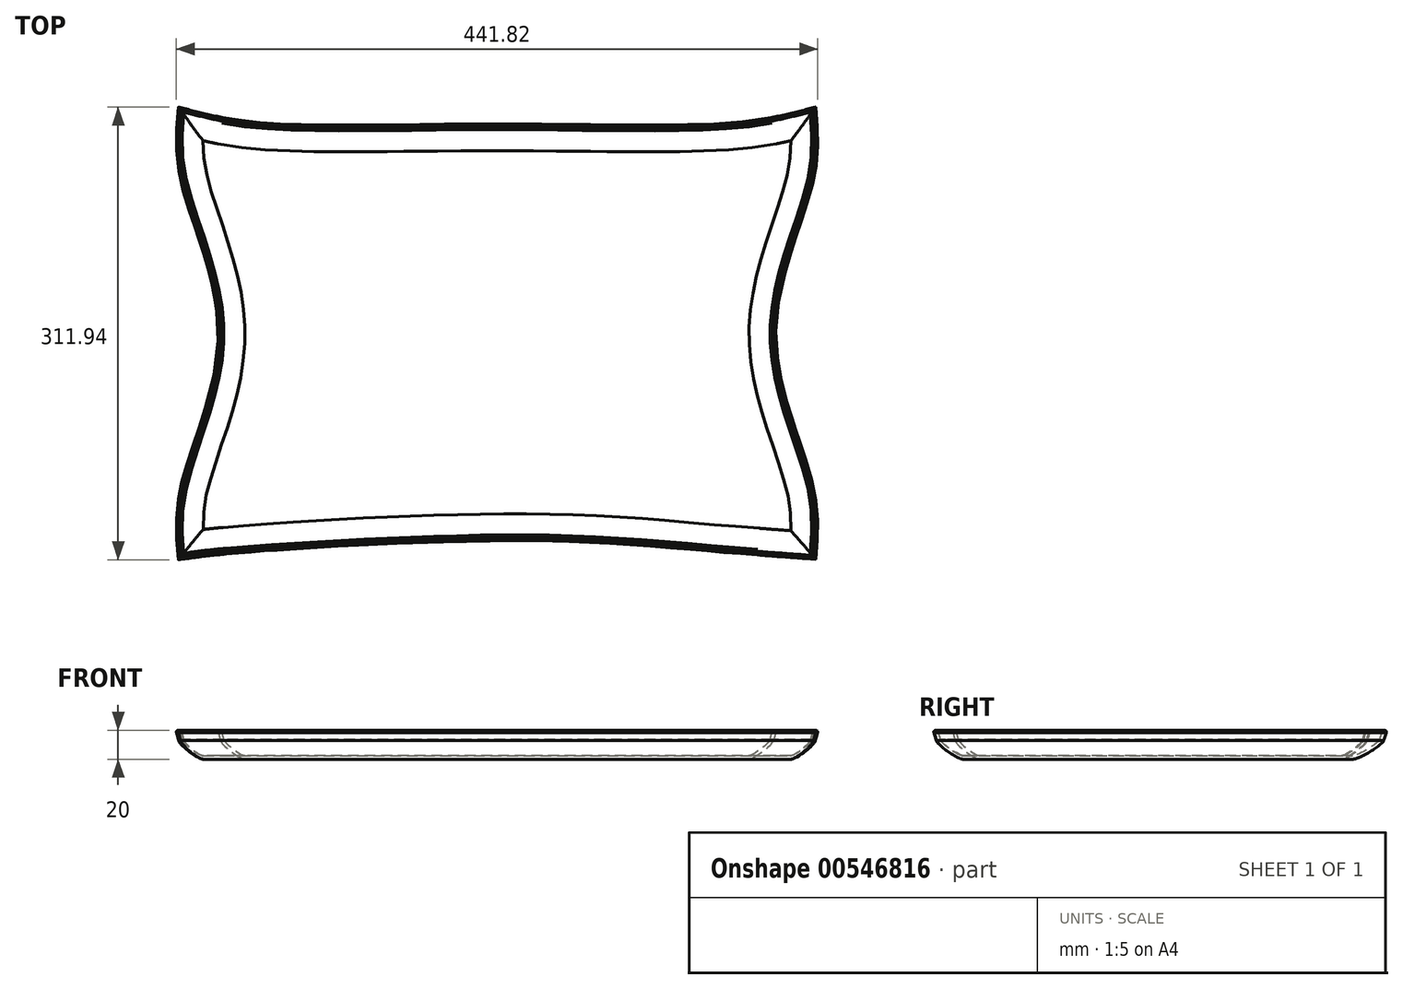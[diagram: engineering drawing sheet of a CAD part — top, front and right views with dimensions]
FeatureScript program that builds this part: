
annotation { "Feature Type Name" : "Feature", "Feature Type Description" : "" }
export const myFeature = defineFeature(function(context is Context, id is Id, definition is map)
    precondition{}
    {
        {
            var Q0;
            Q0=qCreatedBy(makeId("Top.planeOp"),FACE);
            var sketch = newSketch(context, id + "F0", { "sketchPlane" : qUnion([Q0])});
            skFitSpline(sketch, "E0", {"points": [v(-215, 150) * mm, v(-200, 0) * mm, v(-215, -150) * mm], "startDerivative": vector(12.45, -265.1) * mm, "endDerivative": vector(-12.45, -265.1) * mm});
            skLineSegment(sketch, "E1", {"start": v(0, 0) * mm, "end": v(-102.7, 0) * mm, "construction": true});
            skLineSegment(sketch, "E2", {"start": v(0, 0) * mm, "end": v(0, 245.04) * mm, "construction": true});
            skFitSpline(sketch, "E3.MirrorCS", {"points": [v(215, 150) * mm, v(200, 0) * mm, v(215, -150) * mm], "startDerivative": vector(-12.45, -265.1) * mm, "endDerivative": vector(12.45, -265.1) * mm});
            skFitSpline(sketch, "E4", {"points": [v(-215, 150) * mm, v(0, 140.22) * mm, v(215, 150) * mm], "startDerivative": vector(302.65, -55.49) * mm, "endDerivative": vector(302.65, 55.49) * mm});
            skFitSpline(sketch, "E5", {"points": [v(-215, -150) * mm, v(0, -141.43) * mm, v(215, -150) * mm], "startDerivative": vector(199.47, 22.4) * mm, "endDerivative": vector(430, -33.3) * mm});
            skPoint(sketch, "E6", {"position": v(0, 122.52) * mm});
            skSolve(sketch);
        }
        {
            var Q0;
            Q0=qCreatedBy(makeId("Top.planeOp"),FACE);
            var sketch = newSketch(context, id + "F1", { "sketchPlane" : qUnion([Q0])});
            skFitSpline(sketch, "E7.0", {"points": [v(215, -150) * mm, v(212.93, -105.82) * mm, v(187.07, 0) * mm, v(212.93, 105.82) * mm, v(215, 150) * mm]});
            skFitSpline(sketch, "E7.1", {"points": [v(-215, -150) * mm, v(-181.76, -146.27) * mm, v(19.21, -137.5) * mm, v(143.33, -144.45) * mm, v(215, -150) * mm]});
            skFitSpline(sketch, "E7.2", {"points": [v(-215, 150) * mm, v(-212.93, 105.82) * mm, v(-187.07, 0) * mm, v(-212.93, -105.82) * mm, v(-215, -150) * mm]});
            skFitSpline(sketch, "E7.3", {"points": [v(215, 150) * mm, v(164.56, 140.75) * mm, v(0, 139.68) * mm, v(-164.56, 140.75) * mm, v(-215, 150) * mm]});
            skPoint(sketch, "E8.visualSharp", {"position": v(215, 150) * mm});
            skArc(sketch, "E8.filletArc", {"start": v(211.29, 111.47) * mm, "mid": v(203.11, 136.17) * mm, "end": v(178.71, 145.2) * mm});
            skPoint(sketch, "E9.visualSharp", {"position": v(215, -150) * mm});
            skArc(sketch, "E9.filletArc", {"start": v(179.73, -147.4) * mm, "mid": v(203.62, -138.07) * mm, "end": v(211.57, -113.69) * mm});
            skPoint(sketch, "E10.visualSharp", {"position": v(-215, -150) * mm});
            skArc(sketch, "E10.filletArc", {"start": v(-211.54, -113.48) * mm, "mid": v(-203.67, -137.8) * mm, "end": v(-179.93, -147.22) * mm});
            skPoint(sketch, "E11.visualSharp", {"position": v(-215, 150) * mm});
            skArc(sketch, "E11.filletArc", {"start": v(-178.71, 145.2) * mm, "mid": v(-203.11, 136.17) * mm, "end": v(-211.29, 111.47) * mm});
            skSolve(sketch);
        }
        {
            var Q0;
            Q0=qCreatedBy(makeId("Front.planeOp"),FACE);
            var sketch = newSketch(context, id + "F2", { "sketchPlane" : qUnion([Q0])});
            skFitSpline(sketch, "E12", {"points": [v(-200, 0) * mm, v(-188.06, -11.18) * mm, v(0, -22.58) * mm], "startDerivative": vector(27.31, -89.51) * mm, "endDerivative": vector(299, 3.02) * mm});
            skLineSegment(sketch, "E13", {"start": v(0, 0) * mm, "end": v(0, -66.44) * mm, "construction": true});
            skFitSpline(sketch, "E14.MirrorCS", {"points": [v(200, 0) * mm, v(188.06, -11.18) * mm, v(0, -22.58) * mm], "startDerivative": vector(-27.31, -89.51) * mm, "endDerivative": vector(-299, 3.02) * mm});
            skSolve(sketch);
        }
        {
            var Q0;
            Q0 = qSketchRegion(id + "F1", true);
            extrude(context, id + "F3", {"entities" : qUnion([Q0]), "depth" : 20 * mm, "offsetDistance" : 25 * mm, "hasDraft" : true, "draftAngle" : 15 * degree});
        }
        {
            var Q0;
            Q0=makeQuery(id+"F3.opExtrude","CAP_FACE",FACE,{"disambiguationData":[OSD([sQuery(id+"F1.wireOp",EDGE,"E7.0"),sQuery(id+"F1.wireOp",EDGE,"E7.1"),sQuery(id+"F1.wireOp",EDGE,"E7.2"),sQuery(id+"F1.wireOp",EDGE,"E7.3"),sQuery(id+"F1.wireOp",EDGE,"E8.filletArc"),sQuery(id+"F1.wireOp",EDGE,"E9.filletArc"),sQuery(id+"F1.wireOp",EDGE,"E10.filletArc"),sQuery(id+"F1.wireOp",EDGE,"E11.filletArc")])],"isStart":false});
            shell(context, id + "F4", {"entities" : qUnion([Q0]), "thickness" : 2.5 * mm});
        }
        {
            var Q0;
            Q0=makeQuery(id+"F4.opShell","OFFSET_FACE",FACE,{"disambiguationData":[OSD([sQuery(id+"F1.wireOp",EDGE,"E7.0"),sQuery(id+"F1.wireOp",EDGE,"E7.1"),sQuery(id+"F1.wireOp",EDGE,"E7.2"),sQuery(id+"F1.wireOp",EDGE,"E7.3"),sQuery(id+"F1.wireOp",EDGE,"E8.filletArc"),sQuery(id+"F1.wireOp",EDGE,"E9.filletArc"),sQuery(id+"F1.wireOp",EDGE,"E10.filletArc"),sQuery(id+"F1.wireOp",EDGE,"E11.filletArc")])]});
            fillet(context, id + "F5", {"entities" : qUnion([Q0]), "radius" : 15 * mm, "tangentPropagation" : true, "rho" : 0.2, "crossSection" : FilletCrossSection.CONIC, "allowEdgeOverflow" : false});
        }
        {
            var Q0;
            Q0=makeQuery(id+"F3.opExtrude","CAP_FACE",FACE,{"disambiguationData":[OSD([sQuery(id+"F1.wireOp",EDGE,"E7.0"),sQuery(id+"F1.wireOp",EDGE,"E7.1"),sQuery(id+"F1.wireOp",EDGE,"E7.2"),sQuery(id+"F1.wireOp",EDGE,"E7.3"),sQuery(id+"F1.wireOp",EDGE,"E8.filletArc"),sQuery(id+"F1.wireOp",EDGE,"E9.filletArc"),sQuery(id+"F1.wireOp",EDGE,"E10.filletArc"),sQuery(id+"F1.wireOp",EDGE,"E11.filletArc")])],"isStart":true});
            fillet(context, id + "F6", {"entities" : qUnion([Q0]), "radius" : 17.5 * mm, "tangentPropagation" : true, "rho" : 0.2, "crossSection" : FilletCrossSection.CONIC, "allowEdgeOverflow" : false});
        }
        {
            var Q0;
            Q0=makeQuery(id+"F3.opExtrude","CAP_FACE",FACE,{"disambiguationData":[OSD([sQuery(id+"F1.wireOp",EDGE,"E7.0"),sQuery(id+"F1.wireOp",EDGE,"E7.1"),sQuery(id+"F1.wireOp",EDGE,"E7.2"),sQuery(id+"F1.wireOp",EDGE,"E7.3"),sQuery(id+"F1.wireOp",EDGE,"E8.filletArc"),sQuery(id+"F1.wireOp",EDGE,"E9.filletArc"),sQuery(id+"F1.wireOp",EDGE,"E10.filletArc"),sQuery(id+"F1.wireOp",EDGE,"E11.filletArc")])],"isStart":false});
            fillet(context, id + "F7", {"entities" : qUnion([Q0]), "radius" : 1.25 * mm, "tangentPropagation" : true, "allowEdgeOverflow" : false});
        }
    });
